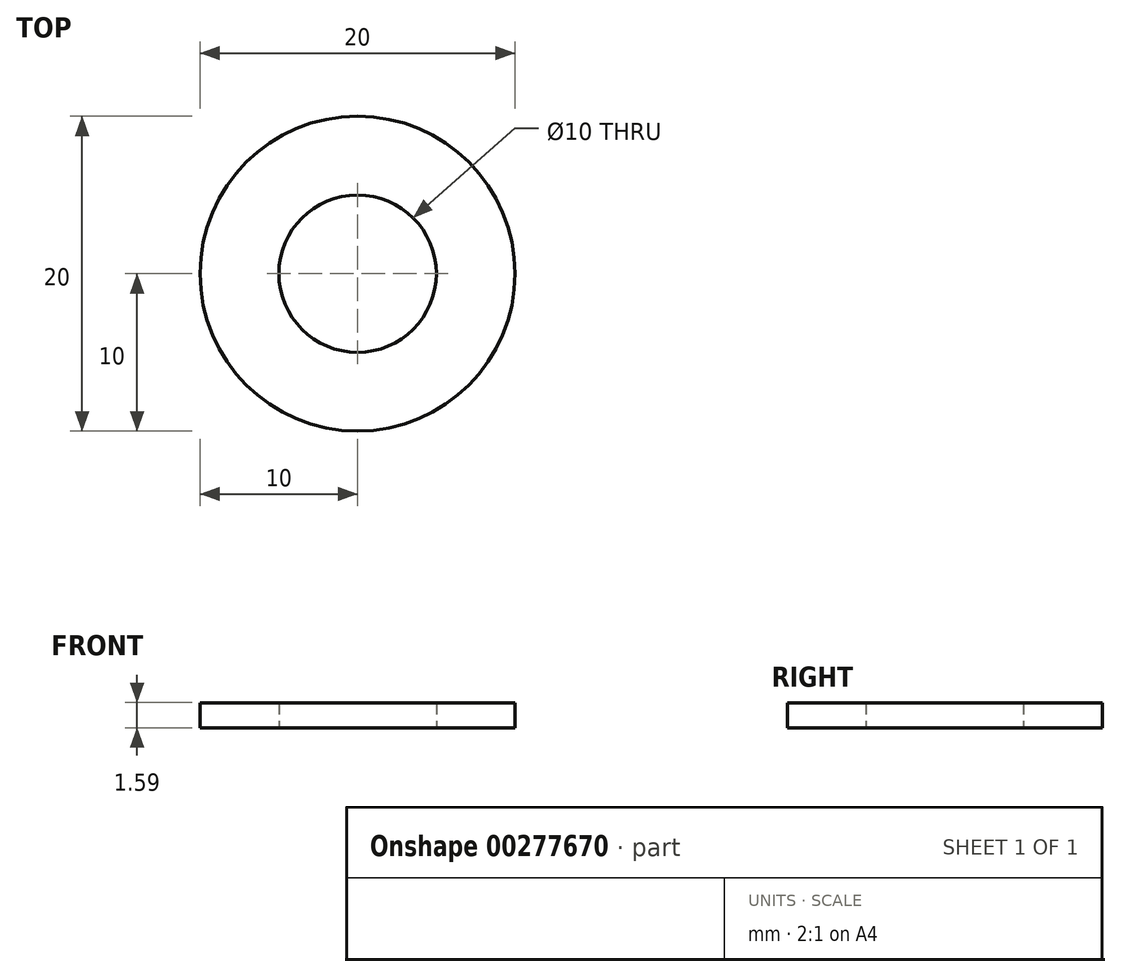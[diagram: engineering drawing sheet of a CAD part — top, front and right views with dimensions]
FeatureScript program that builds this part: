
annotation { "Feature Type Name" : "Feature", "Feature Type Description" : "" }
export const myFeature = defineFeature(function(context is Context, id is Id, definition is map)
    precondition{}
    {
        {
            var Q0;
            Q0=qCreatedBy(makeId("Top.planeOp"),FACE);
            var sketch = newSketch(context, id + "F0", { "sketchPlane" : qUnion([Q0])});
            skCircle(sketch, "E0", {"center": v(0, 0) * mm, "radius": 10 * mm});
            skCircle(sketch, "E1", {"center": v(0, 0) * mm, "radius": 5 * mm});
            skSolve(sketch);
        }
        {
            var Q0;
            Q0=makeQuery(id+"F0.imprint","IMPRINT",FACE,{"disambiguationData":[TD([[makeQuery(id+"F0.imprint","IMPRINT",EDGE,{"derivedFrom":sQuery(id+"F0.wireOp",EDGE,"E0")}),1.0]])]});
            extrude(context, id + "F1", {"entities" : qUnion([Q0]), "depth" : 1.59 * mm});
        }
    });
